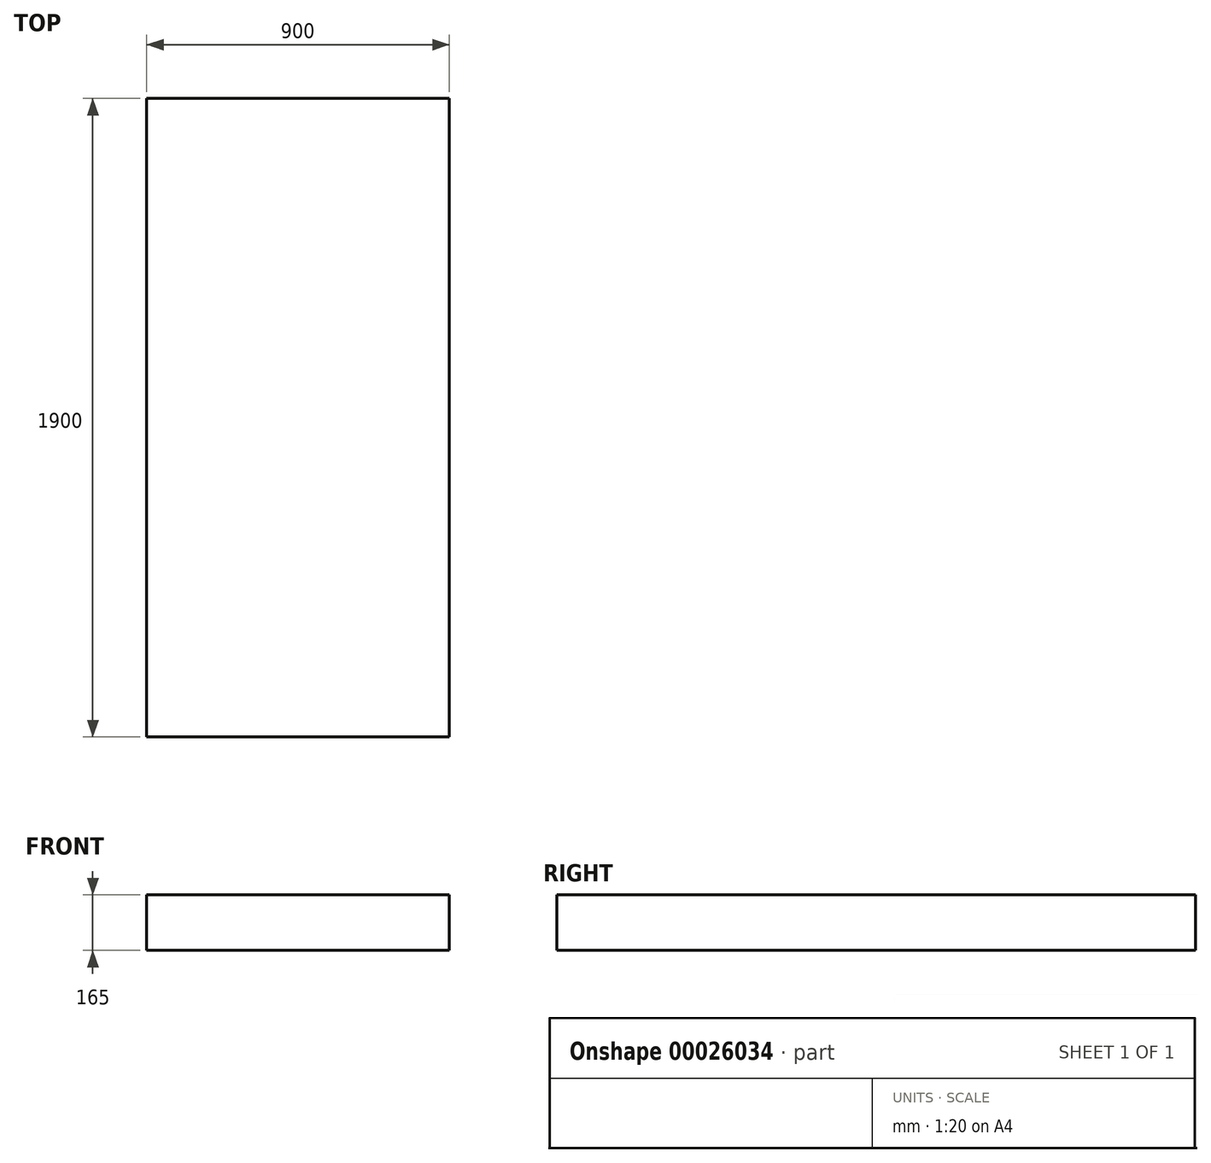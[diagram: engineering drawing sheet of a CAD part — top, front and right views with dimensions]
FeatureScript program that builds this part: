
annotation { "Feature Type Name" : "Feature", "Feature Type Description" : "" }
export const myFeature = defineFeature(function(context is Context, id is Id, definition is map)
    precondition{}
    {
        {
            var Q0;
            Q0=qCreatedBy(makeId("Front.planeOp"),FACE);
            var sketch = newSketch(context, id + "F0", { "sketchPlane" : qUnion([Q0])});
            skLineSegment(sketch, "E0.bottom", {"start": v(0, 0) * mm, "end": v(900, 0) * mm});
            skLineSegment(sketch, "E0.top", {"start": v(0, 165) * mm, "end": v(900, 165) * mm});
            skLineSegment(sketch, "E0.left", {"start": v(0, 0) * mm, "end": v(0, 165) * mm});
            skLineSegment(sketch, "E0.right", {"start": v(900, 0) * mm, "end": v(900, 165) * mm});
            skSolve(sketch);
        }
        {
            var Q0;
            Q0 = qSketchRegion(id + "F0", true);
            extrude(context, id + "F1", {"entities" : qUnion([Q0]), "depth" : 1900 * mm});
        }
    });
